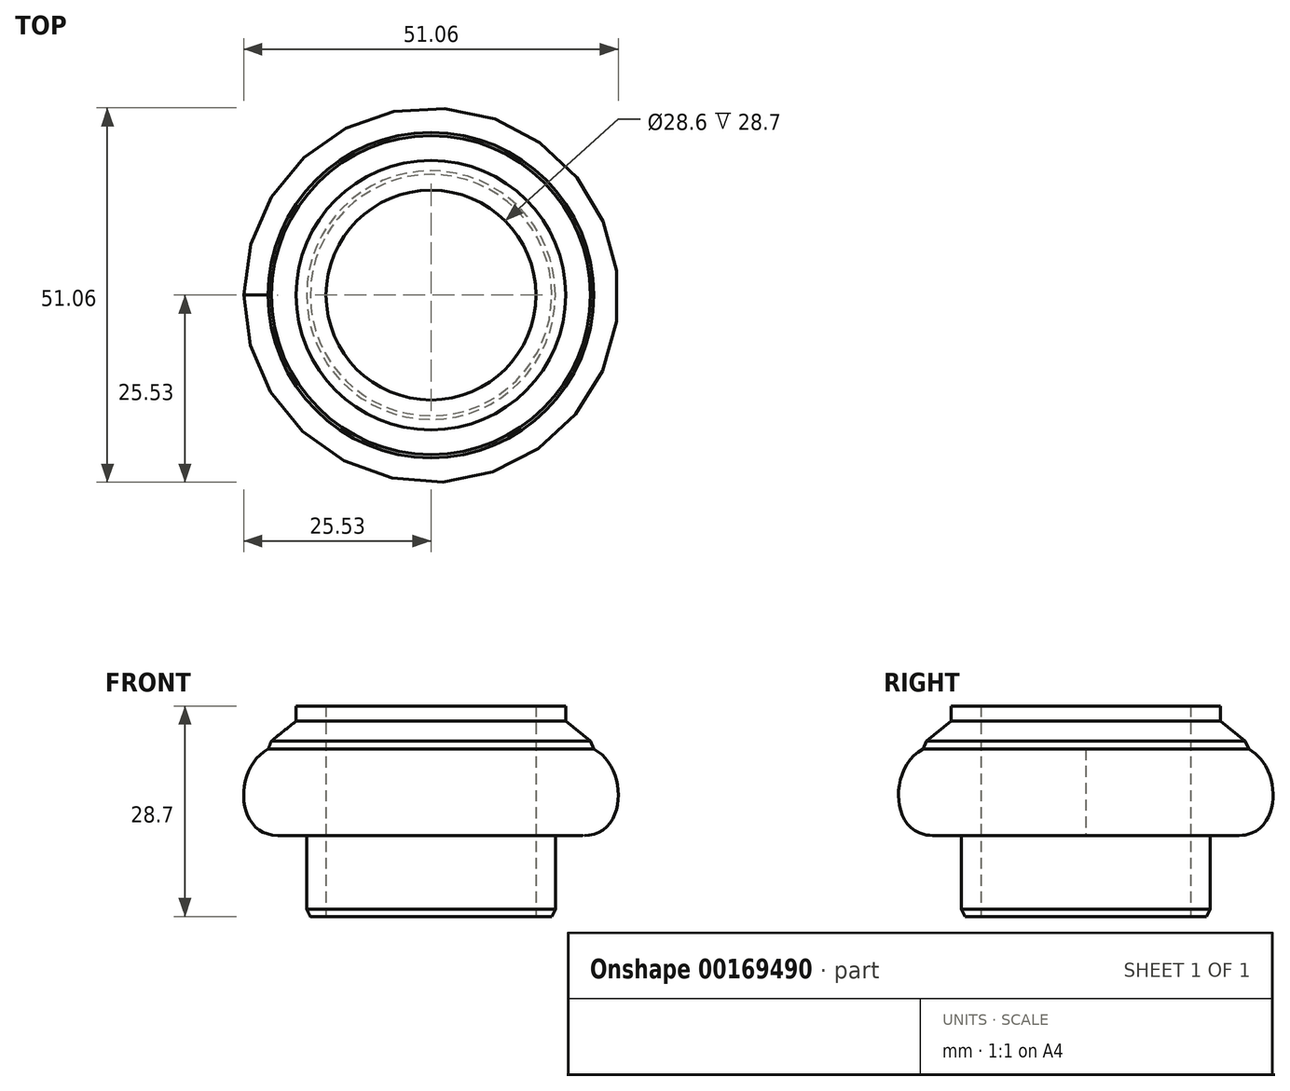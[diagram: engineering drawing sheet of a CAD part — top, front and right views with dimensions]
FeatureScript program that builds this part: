
annotation { "Feature Type Name" : "Feature", "Feature Type Description" : "" }
export const myFeature = defineFeature(function(context is Context, id is Id, definition is map)
    precondition{}
    {
        {
            var Q0;
            Q0=qCreatedBy(makeId("Front.planeOp"),FACE);
            var sketch = newSketch(context, id + "F0", { "sketchPlane" : qUnion([Q0])});
            skLineSegment(sketch, "E0", {"start": v(0, 0) * mm, "end": v(-16.95, 0) * mm, "construction": true});
            skLineSegment(sketch, "E1", {"start": v(-16.95, 0) * mm, "end": v(-16.95, 11.06) * mm});
            skLineSegment(sketch, "E2", {"start": v(-16.95, 11.06) * mm, "end": v(-20.87, 11.06) * mm});
            skLineSegment(sketch, "E3", {"start": v(0, 0) * mm, "end": v(0, 28.7) * mm, "construction": true});
            skLineSegment(sketch, "E4", {"start": v(0, 28.7) * mm, "end": v(-14.3, 28.7) * mm, "construction": true});
            skLineSegment(sketch, "E5", {"start": v(-14.3, 28.7) * mm, "end": v(-14.3, 0) * mm});
            skLineSegment(sketch, "E6", {"start": v(-14.3, 0) * mm, "end": v(-16.95, 0) * mm});
            skLineSegment(sketch, "E7", {"start": v(-14.3, 28.7) * mm, "end": v(-18.37, 28.7) * mm});
            skLineSegment(sketch, "E8", {"start": v(-18.37, 28.7) * mm, "end": v(-18.37, 26.66) * mm});
            skLineSegment(sketch, "E9", {"start": v(-18.37, 26.66) * mm, "end": v(-21.74, 23.95) * mm});
            skLineSegment(sketch, "E10", {"start": v(-21.74, 23.95) * mm, "end": v(-22.19, 22.83) * mm});
            skFitSpline(sketch, "E11", {"points": [v(-22.19, 22.83) * mm, v(-20.87, 11.06) * mm], "startDerivative": vector(-14.14, -7.4) * mm, "endDerivative": vector(17.68, 0.07) * mm});
            skSolve(sketch);
        }
        {
            var Q0;
            Q0=makeQuery(id+"F0.imprint","IMPRINT",FACE,{"disambiguationData":[TD([[makeQuery(id+"F0.imprint","IMPRINT",EDGE,{"derivedFrom":sQuery(id+"F0.wireOp",EDGE,"E1")}),-1.0]])]});
            var Q1;
            Q1=sQuery(id+"F0.wireOp",EDGE,"E3");
            revolve(context, id + "F1", {"entities" : qUnion([Q0]), "axis" : qUnion([Q1]), "revolveType" : RevolveType.FULL});
        }
        {
            var Q0;
            Q0=makeQuery(id+"F1.opRevolve","SWEPT_EDGE",EDGE,{"disambiguationData":[OSD([sQuery(id+"F0.wireOp",EDGE,"E1"),sQuery(id+"F0.wireOp",EDGE,"E6")])]});
            chamfer(context, id + "F2", {"entities" : qUnion([Q0]), "chamferType" : ChamferType.TWO_OFFSETS, "width1" : .5 * mm, "oppositeDirection" : false, "width2" : 1 * mm, "tangentPropagation" : true});
        }
    });
